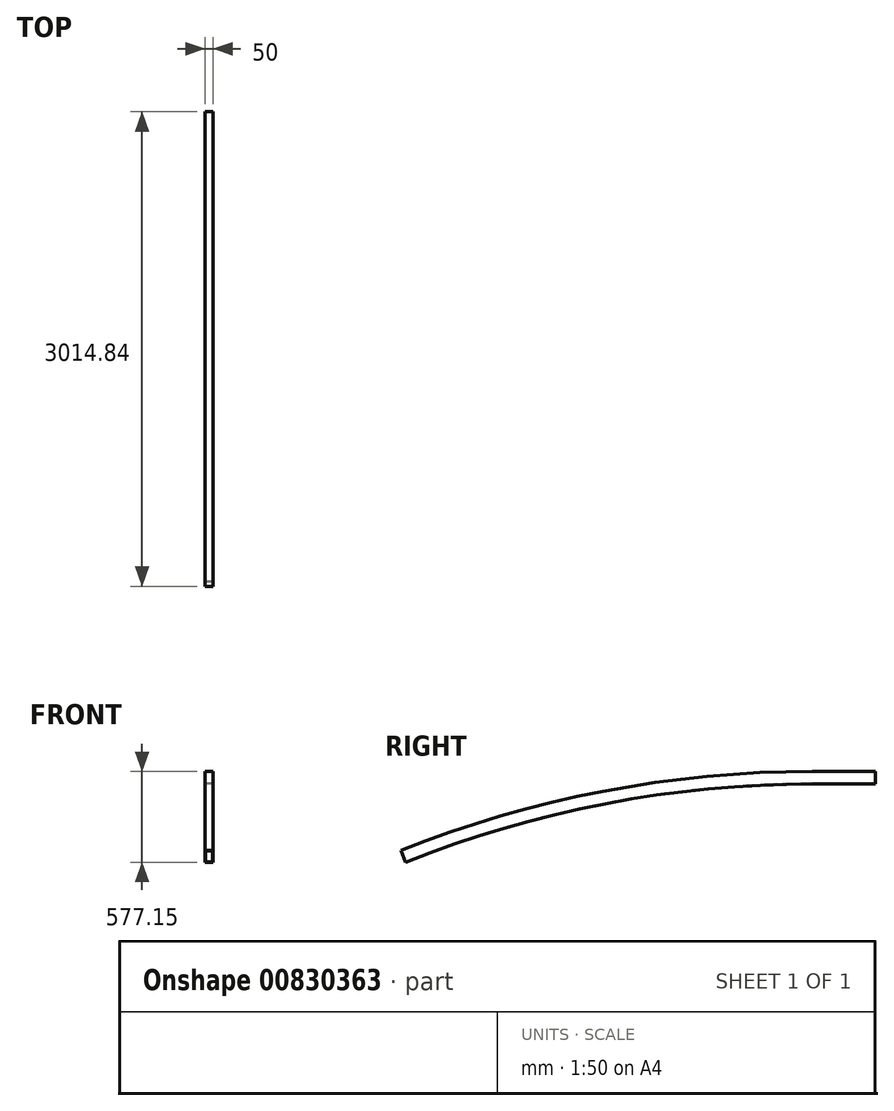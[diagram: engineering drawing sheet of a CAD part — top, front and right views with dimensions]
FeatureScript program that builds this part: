
annotation { "Feature Type Name" : "Feature", "Feature Type Description" : "" }
export const myFeature = defineFeature(function(context is Context, id is Id, definition is map)
    precondition{}
    {
        {
            var Q0;
            Q0=qCreatedBy(makeId("Front.planeOp"),FACE);
            var sketch = newSketch(context, id + "F0", { "sketchPlane" : qUnion([Q0])});
            skLineSegment(sketch, "E0.bottom", {"start": v(25, 40) * mm, "end": v(-25, 40) * mm});
            skLineSegment(sketch, "E0.top", {"start": v(25, -40) * mm, "end": v(-25, -40) * mm});
            skLineSegment(sketch, "E0.left", {"start": v(25, 40) * mm, "end": v(25, -40) * mm});
            skLineSegment(sketch, "E0.right", {"start": v(-25, 40) * mm, "end": v(-25, -40) * mm});
            skPoint(sketch, "E0.middle", {"position": v(0, 0) * mm});
            skLineSegment(sketch, "E1.0", {"start": v(-22, 37) * mm, "end": v(-22, -37) * mm});
            skLineSegment(sketch, "E1.1", {"start": v(22, 37) * mm, "end": v(-22, 37) * mm});
            skLineSegment(sketch, "E1.2", {"start": v(22, 37) * mm, "end": v(22, -37) * mm});
            skLineSegment(sketch, "E1.3", {"start": v(22, -37) * mm, "end": v(-22, -37) * mm});
            skSolve(sketch);
        }
        {
            var Q0;
            Q0=qCreatedBy(makeId("Right.planeOp"),FACE);
            var sketch = newSketch(context, id + "F1", { "sketchPlane" : qUnion([Q0])});
            skLineSegment(sketch, "E2", {"start": v(0, 0) * mm, "end": v(-400, 0) * mm});
            skArc(sketch, "E3", {"start": v(-400, 0) * mm, "mid": v(-1723.82, -126.13) * mm, "end": v(-3000, -500) * mm});
            skLineSegment(sketch, "E4", {"start": v(-400, 0) * mm, "end": v(-3000, 0) * mm, "construction": true});
            skLineSegment(sketch, "E5", {"start": v(-3000, 0) * mm, "end": v(-3000, -500) * mm, "construction": true});
            skSolve(sketch);
        }
        {
            var Q0;
            Q0 = qSketchRegion(id + "F0", true);
            var Q1;
            Q1 = qConstructionFilter(qBodyType(qCreatedBy(id + "F1" ,EDGE), BodyType.WIRE), ConstructionObject.NO);
            sweep(context, id + "F2", {"profiles" : qUnion([Q0]), "path" : qUnion([Q1])});
        }
    });
